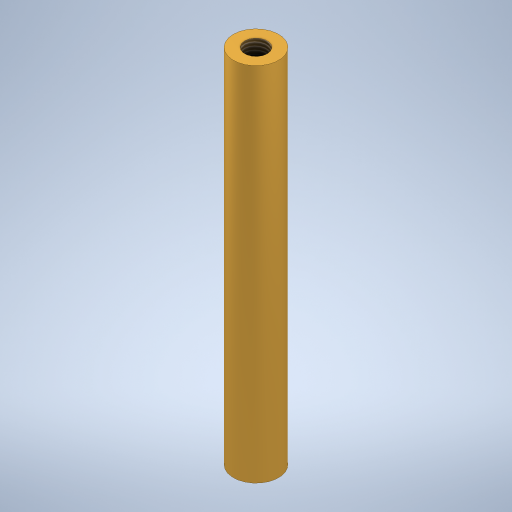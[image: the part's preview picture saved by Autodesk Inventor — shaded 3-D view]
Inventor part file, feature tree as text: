
AUTODESK INVENTOR PART (.ipt)
format: ipt  version: 2023.2 (Build 272271030, 271C)  size: 249,344 bytes
history: native  units: mm
features: extrude x2, sketch x2, other x1, thread x1
ambient origin geometry x8: Origin, YZ Plane, XZ Plane, XY Plane, X Axis, Y Axis, Z Axis, Center Point
bodies: Body1 (feature_tree)
feature tree (6):
  other  "Sólido1"
  extrude  "Extrusão1"  Depth=80.0mm TaperAngle=0.0deg
  extrude  "Extrusão2"  Depth=15.0mm TaperAngle=0.0deg
  thread  "Rosca1"  [1 undecoded]
  sketch  "Esboço1"  dims[d0=10.0mm d2=80.0mm d3=0.0mm]
  sketch  "Esboço2"  dims[d4=5.0mm d5=15.0mm d6=0.0mm d7=15.0mm d8=0.0mm]
note: 1 required parameter value undecoded (feature->parameter linkage not recoverable at this tier; creation-order binding heuristic only, values carry confidence <= 0.55)
